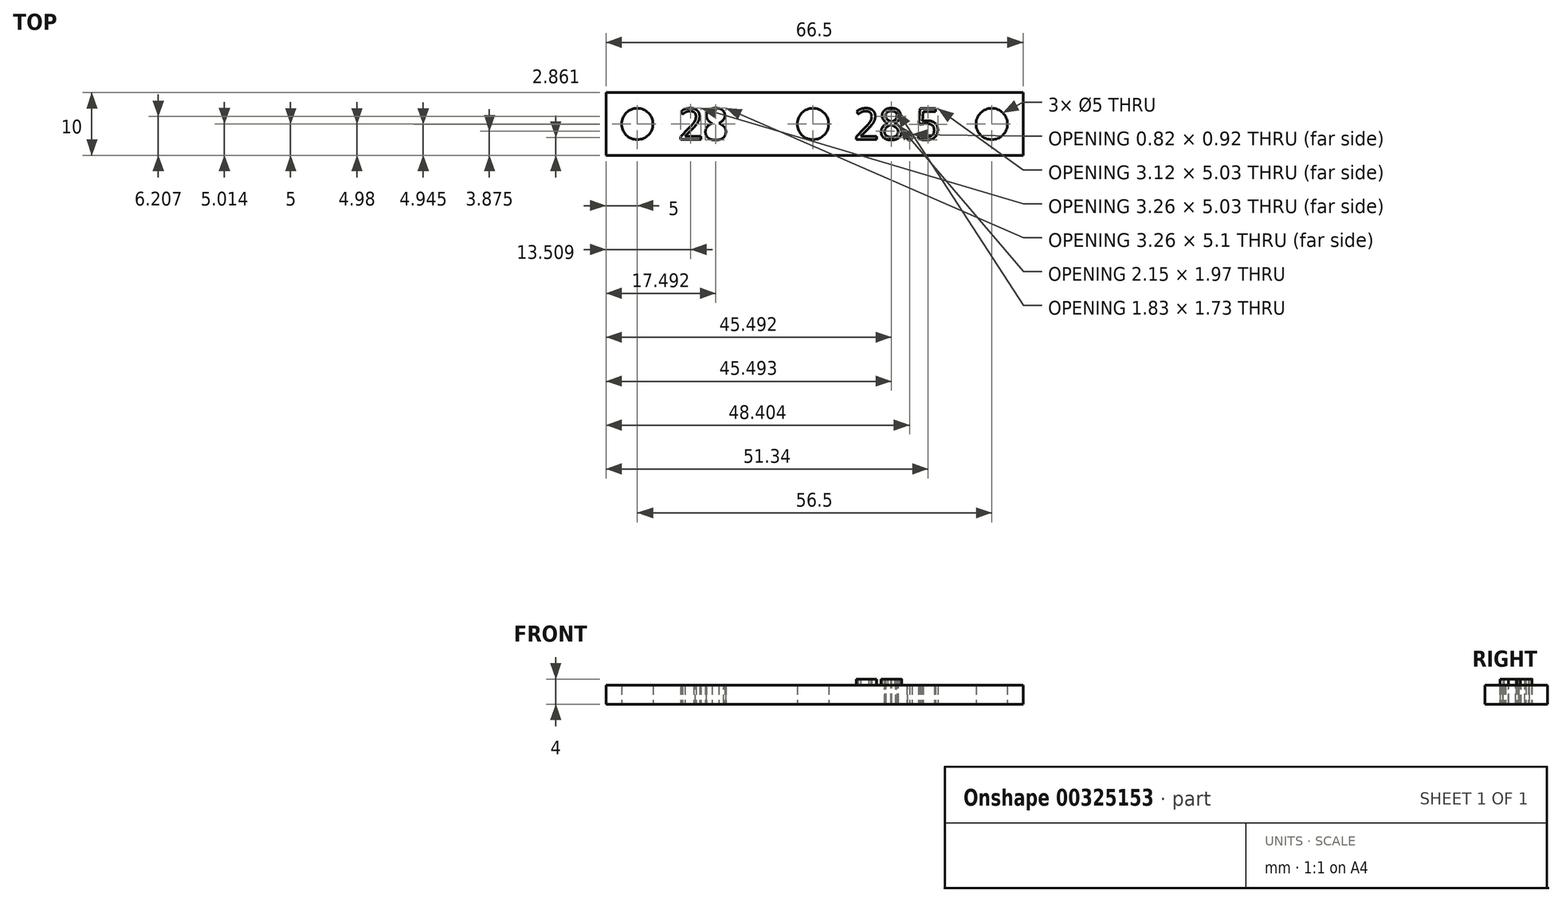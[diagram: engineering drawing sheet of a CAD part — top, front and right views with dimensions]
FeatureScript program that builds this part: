
annotation { "Feature Type Name" : "Feature", "Feature Type Description" : "" }
export const myFeature = defineFeature(function(context is Context, id is Id, definition is map)
    precondition{}
    {
        {
            var Q0;
            Q0=qCreatedBy(makeId("Top.planeOp"),FACE);
            var sketch = newSketch(context, id + "F0", { "sketchPlane" : qUnion([Q0])});
            skLineSegment(sketch, "E0", {"start": v(0, 0) * mm, "end": v(28.5, 0) * mm, "construction": true});
            skText(sketch, "E1", { "text": "28.5", "fontName": "OpenSans-Regular.ttf"});
            skCircle(sketch, "E2", {"center": v(0, 0) * mm, "radius": 2.5 * mm});
            skCircle(sketch, "E3", {"center": v(28.5, 0) * mm, "radius": 2.5 * mm});
            skLineSegment(sketch, "E4", {"start": v(0, 0) * mm, "end": v(-28, 0) * mm, "construction": true});
            skLineSegment(sketch, "E5", {"start": v(-28, 0) * mm, "end": v(-33, 0) * mm, "construction": true});
            skText(sketch, "E6", { "text": "28\n", "fontName": "OpenSans-Regular.ttf"});
            skLineSegment(sketch, "E7", {"start": v(0, 0) * mm, "end": v(6.54, 2.5) * mm, "construction": true});
            skLineSegment(sketch, "E8", {"start": v(0, 0) * mm, "end": v(6.54, -2.5) * mm, "construction": true});
            skLineSegment(sketch, "E9", {"start": v(-28, 0) * mm, "end": v(-21.46, 2.5) * mm, "construction": true});
            skLineSegment(sketch, "E10", {"start": v(-21.46, -2.5) * mm, "end": v(-28, 0) * mm, "construction": true});
            skCircle(sketch, "E11", {"center": v(-28, 0) * mm, "radius": 2.5 * mm});
            skLineSegment(sketch, "E12", {"start": v(-33, 0) * mm, "end": v(-33, 5) * mm});
            skLineSegment(sketch, "E13", {"start": v(-33, 0) * mm, "end": v(-33, -5) * mm});
            skLineSegment(sketch, "E14", {"start": v(28.5, 0) * mm, "end": v(33.5, 0) * mm, "construction": true});
            skLineSegment(sketch, "E15", {"start": v(33.5, 0) * mm, "end": v(33.5, 5) * mm});
            skLineSegment(sketch, "E16", {"start": v(33.5, 0) * mm, "end": v(33.5, -5) * mm});
            skLineSegment(sketch, "E17", {"start": v(33.5, 5) * mm, "end": v(-33, 5) * mm});
            skLineSegment(sketch, "E18", {"start": v(-33, -5) * mm, "end": v(33.5, -5) * mm});
            const initialGuessF0  = {"E1": [0.00654, -0.0025, 1, 0, 0.005], "E6": [-0.02146, -0.0025, 1, 0, 0.005]};
            skSetInitialGuess(sketch, initialGuessF0);
            skSolve(sketch);
        }
        {
            var Q0;
            Q0=makeQuery(id+"F0.imprint","IMPRINT",FACE,{"disambiguationData":[TD([[makeQuery(id+"F0.imprint","IMPRINT",EDGE,{"derivedFrom":sQuery(id+"F0.wireOp",EDGE,"E1.sketch_text.stroke-0")}),1.0]])]});
            extrude(context, id + "F1", {"entities" : qUnion([Q0]), "depth" : 3 * mm});
        }
        {
            var Q0;
            Q0=makeQuery(id+"F0.imprint","IMPRINT",FACE,{"disambiguationData":[TD([[makeQuery(id+"F0.imprint","IMPRINT",EDGE,{"derivedFrom":sQuery(id+"F0.wireOp",EDGE,"E1.sketch_text.stroke-0")}),-1.0]])]});
            var Q1;
            Q1=makeQuery(id+"F0.imprint","IMPRINT",FACE,{"disambiguationData":[TD([[makeQuery(id+"F0.imprint","IMPRINT",EDGE,{"derivedFrom":sQuery(id+"F0.wireOp",EDGE,"E1.sketch_text.stroke-27")}),-1.0]])]});
            var Q2;
            Q2=makeQuery(id+"F0.imprint","IMPRINT",FACE,{"disambiguationData":[TD([[makeQuery(id+"F0.imprint","IMPRINT",EDGE,{"derivedFrom":sQuery(id+"F0.wireOp",EDGE,"E1.sketch_text.stroke-35")}),-1.0]])]});
            var Q3;
            Q3=makeQuery(id+"F0.imprint","IMPRINT",FACE,{"disambiguationData":[TD([[makeQuery(id+"F0.imprint","IMPRINT",EDGE,{"derivedFrom":sQuery(id+"F0.wireOp",EDGE,"E1.sketch_text.stroke-20")}),-1.0]])]});
            extrude(context, id + "F2", {"entities" : qUnion([Q0, Q1, Q2, Q3]), "operationType" : NewBodyOperationType.ADD, "depth" : 4 * mm});
        }
    });
